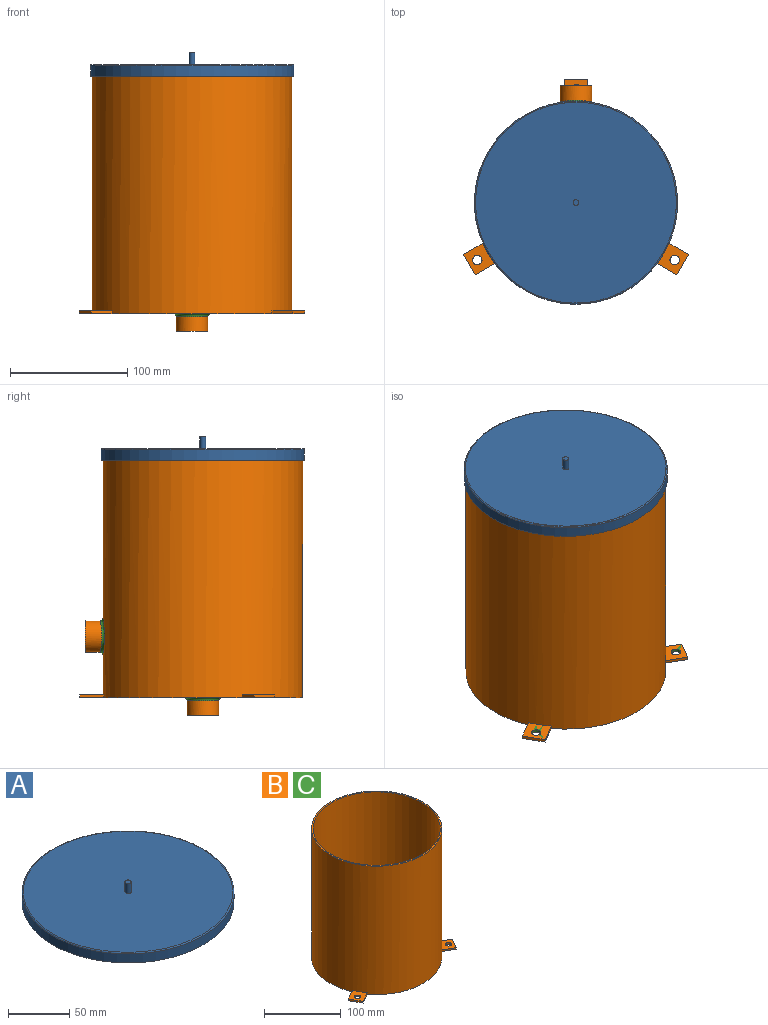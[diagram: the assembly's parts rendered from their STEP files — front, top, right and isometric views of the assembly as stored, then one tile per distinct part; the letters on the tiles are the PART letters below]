
ASSEMBLY  parts=3 mates=1
PART A: 8 faces, bbox 187.3x187.3x20 mm
  f0: cylinder r=86.5mm len=173mm, axis (0,0,-1), area 4891.5mm2, adj f2,f7
  f1: plane 171x171mm, normal (0,0,1), area 22946.2mm2, adj f5,f7
  f2: plane 173x173mm, normal (0,0,-1), area 540.4mm2, adj f0,f3
  f3: cylinder r=85.5mm len=171mm, axis (0,0,-1), area 4834.9mm2, adj f2,f4
  f4: plane 171x171mm, normal (0,0,-1), area 22965.8mm2, adj f3
  f5: cylinder r=2.5mm len=10mm, axis (0,0,-1), area 157.1mm2, adj f1,f6
  f6: plane 5x5mm, normal (0,0,1), area 19.6mm2, adj f5
  f7: torus R=85.5mm, axis (0,0,1), area 850.1mm2, adj f0,f1
PART B: 28 faces, bbox 191.9x190x220 mm
  f0: cylinder r=85mm len=205mm, axis (0,0,-1), area 108548.5mm2, adj f1,f2,f4,f6,f7,f9,f11,f12
  f1: plane 191.87x190mm, normal (0,0,-1), area 22954.8mm2, adj f0,f2,f3,f4,f5,f7,f8,f9
  f2: plane 20.59x2.5mm, normal (1,0,0), area 51.5mm2, adj f0,f1,f3,f6
  f3: plane 20x2.5mm, normal (0,1,0), area 50mm2, adj f1,f2,f4,f6
  f4: plane 20.59x2.5mm, normal (-1,0,0), area 51.5mm2, adj f0,f1,f3,f6
  f5: cylinder r=4mm len=8mm, axis (0,0,-1), area 62.8mm2, adj f1,f6
  f6: plane 20.59x20mm, normal (0,0,1), area 353.7mm2, adj f0,f2,f3,f4,f5
  f7: plane 17.83x10.3mm, normal (-0.5,0.87,0), area 51.5mm2, adj f0,f1,f8,f11
  f8: plane 17.32x10mm, normal (-0.87,-0.5,0), area 50mm2, adj f1,f7,f9,f11
  f9: plane 17.83x10.3mm, normal (0.5,-0.87,0), area 51.5mm2, adj f0,f1,f8,f11
  f10: cylinder r=4mm len=8mm, axis (0,0,-1), area 62.8mm2, adj f1,f11
  f11: plane 27.83x27.62mm, normal (0,0,1), area 353.7mm2, adj f0,f7,f8,f9,f10
  f12: plane 17.83x10.3mm, normal (-0.5,-0.87,0), area 51.5mm2, adj f0,f1,f13,f16
  f13: plane 17.32x10mm, normal (0.87,-0.5,0), area 50mm2, adj f1,f12,f14,f16
  f14: plane 17.83x10.3mm, normal (0.5,0.87,0), area 51.5mm2, adj f0,f1,f13,f16
  f15: cylinder r=4mm len=8mm, axis (0,0,-1), area 62.8mm2, adj f1,f16
  f16: plane 27.83x27.62mm, normal (0,0,1), area 353.7mm2, adj f0,f12,f13,f14,f15
  f17: cylinder r=83mm len=203mm, axis (0,0,-1), area 105515.1mm2, adj f18,f19,f27
  f18: plane 170x170mm, normal (0,0,1), area 1055.6mm2, adj f0,f17
  f19: plane 166x166mm, normal (0,0,1), area 21296.1mm2, adj f17,f22
  f20: plane 27x27mm, normal (0,0,-1), area 226.2mm2, adj f21,f22
  f21: cylinder r=13.5mm len=27mm, axis (0,0,1), area 1060.3mm2, adj f20,f26
  f22: cylinder r=10.5mm len=21mm, axis (0,0,-1), area 1121.5mm2, adj f19,f20
  f23: cylinder r=13.5mm len=27mm, axis (0,-1,0), area 1122.7mm2, adj f24,f25
  f24: plane 27x27mm, normal (0,1,0), area 226.2mm2, adj f23,f27
  f25: bspline ~32.01x31.1mm, area 333.3mm2, adj f0,f23
  f26: torus R=16mm, axis (0,0,1), area 355.5mm2, adj f1,f21
  f27: cylinder r=10.5mm len=21mm, axis (0,1,0), area 1143.5mm2, adj f17,f24
PART C: same geometry as B
PLACE A t=(-46.48,1.19,164.03)mm
PLACE B t=(-46.48,1.19,-37.97)mm
PLACE C t=(-46.48,1.19,-37.97)mm
MATE slider A.f0 <-> B.f0  axis (0,0,-1) through (-46.48,1.19,168.53)mm
